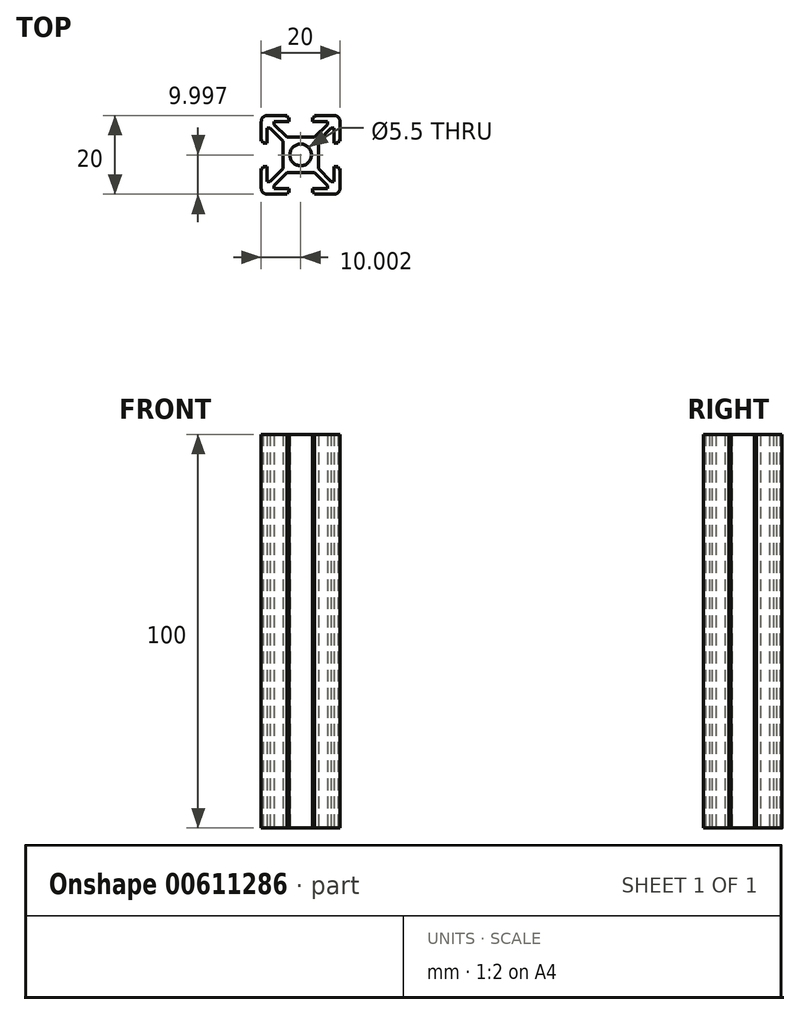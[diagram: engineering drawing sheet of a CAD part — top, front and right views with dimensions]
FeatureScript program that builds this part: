
annotation { "Feature Type Name" : "Feature", "Feature Type Description" : "" }
export const myFeature = defineFeature(function(context is Context, id is Id, definition is map)
    precondition{}
    {
        {
            var Q0;
            Q0=qCreatedBy(makeId("Top.planeOp"),FACE);
            var sketch = newSketch(context, id + "F0", { "sketchPlane" : qUnion([Q0])});
            skLineSegment(sketch, "E0", {"start": v(-1.2, -4.52) * mm, "end": v(-5.7, -4.52) * mm});
            skLineSegment(sketch, "E1", {"start": v(-8.97, -7.8) * mm, "end": v(-8.97, -8.52) * mm});
            skLineSegment(sketch, "E2", {"start": v(-8.97, -8.52) * mm, "end": v(-5.2, -8.52) * mm});
            skLineSegment(sketch, "E3", {"start": v(-5.2, -8.52) * mm, "end": v(-5.2, -9.52) * mm});
            skLineSegment(sketch, "E4", {"start": v(-7.76, -10.02) * mm, "end": v(-10.7, -10.02) * mm});
            skLineSegment(sketch, "E5", {"start": v(-5.2, -9.52) * mm, "end": v(-5.7, -9.52) * mm});
            skLineSegment(sketch, "E6", {"start": v(-5.7, -9.52) * mm, "end": v(-5.7, -10.02) * mm, "construction": true});
            skArc(sketch, "E7.filletArc", {"start": v(-11.76, -9.58) * mm, "mid": v(-11.27, -9.9) * mm, "end": v(-10.7, -10.02) * mm});
            skLineSegment(sketch, "E8", {"start": v(-5.7, -10.02) * mm, "end": v(-7.76, -10.02) * mm});
            skPoint(sketch, "E9.orphan", {"position": v(-2.2, -10.02) * mm});
            skLineSegment(sketch, "E10.trimOffspring", {"start": v(-10.7, -8.52) * mm, "end": v(-4.14, -1.97) * mm});
            skPoint(sketch, "E11", {"position": v(-2.2, -4.52) * mm});
            skLineSegment(sketch, "E12", {"start": v(-5.7, -4.52) * mm, "end": v(-8.97, -7.8) * mm});
            skArc(sketch, "E13", {"start": v(-4.14, -1.97) * mm, "mid": v(-3.25, -2.56) * mm, "end": v(-2.2, -2.77) * mm});
            skPoint(sketch, "E14", {"position": v(-4.14, -1.97) * mm});
            skLineSegment(sketch, "E15", {"start": v(-2.2, -4.02) * mm, "end": v(-2.2, -2.77) * mm});
            skLineSegment(sketch, "E16", {"start": v(-11.76, -9.58) * mm, "end": v(-10.7, -8.52) * mm});
            skPoint(sketch, "E17", {"position": v(-7.76, -10.02) * mm});
            skLineSegment(sketch, "E18", {"start": v(-5.7, -9.52) * mm, "end": v(-5.7, -10.02) * mm});
            skPoint(sketch, "E19.0.MirrorP", {"position": v(-12.2, -5.59) * mm});
            skPoint(sketch, "E19.1.MirrorP", {"position": v(-12.2, -5.59) * mm});
            skPoint(sketch, "E19.2.MirrorP", {"position": v(-12.2, -5.59) * mm});
            skPoint(sketch, "E19.3.MirrorP", {"position": v(-12.2, -5.59) * mm});
            skPoint(sketch, "E19.4.MirrorP", {"position": v(-12.2, -5.59) * mm});
            skPoint(sketch, "E19.5.MirrorP", {"position": v(-12.2, -5.59) * mm});
            skPoint(sketch, "E19.6.MirrorP", {"position": v(-12.2, -5.59) * mm});
            skPoint(sketch, "E19.7.MirrorP", {"position": v(-12.2, -5.59) * mm});
            skPoint(sketch, "E19.8.MirrorP", {"position": v(-12.2, -5.59) * mm});
            skPoint(sketch, "E19.9.MirrorP", {"position": v(-12.2, -5.59) * mm});
            skPoint(sketch, "E19.10.MirrorP", {"position": v(-12.2, -5.59) * mm});
            skLineSegment(sketch, "E19.11.MirrorCS", {"start": v(-11.7, -3.52) * mm, "end": v(-12.2, -3.52) * mm, "construction": true});
            skPoint(sketch, "E19.12.MirrorP", {"position": v(-12.2, -5.59) * mm});
            skLineSegment(sketch, "E19.13.MirrorCS", {"start": v(-11.7, -3.52) * mm, "end": v(-12.2, -3.52) * mm});
            skLineSegment(sketch, "E19.14.MirrorCS", {"start": v(-9.97, -6.8) * mm, "end": v(-10.7, -6.8) * mm});
            skPoint(sketch, "E19.15.MirrorP", {"position": v(-12.2, -5.59) * mm});
            skLineSegment(sketch, "E19.16.MirrorCS", {"start": v(-11.7, -3.02) * mm, "end": v(-11.7, -3.52) * mm});
            skPoint(sketch, "E19.17.MirrorP", {"position": v(-12.2, -0.02) * mm});
            skLineSegment(sketch, "E19.18.MirrorCS", {"start": v(-12.2, -5.59) * mm, "end": v(-12.2, -8.52) * mm});
            skArc(sketch, "E19.19.MirrorCS", {"start": v(-4.14, -1.97) * mm, "mid": v(-4.74, -1.07) * mm, "end": v(-4.95, -0.02) * mm});
            skPoint(sketch, "E19.20.MirrorP", {"position": v(-6.7, -0.02) * mm});
            skLineSegment(sketch, "E19.21.MirrorCS", {"start": v(-6.7, -3.52) * mm, "end": v(-9.97, -6.8) * mm});
            skLineSegment(sketch, "E19.23.MirrorCS", {"start": v(-6.7, -1.02) * mm, "end": v(-6.7, -3.52) * mm});
            skLineSegment(sketch, "E19.24.MirrorCS", {"start": v(-10.7, -6.8) * mm, "end": v(-10.7, -3.02) * mm});
            skLineSegment(sketch, "E19.25.MirrorCS", {"start": v(-12.2, -3.52) * mm, "end": v(-12.2, -5.59) * mm});
            skArc(sketch, "E19.28.MirrorCS", {"start": v(-11.76, -9.58) * mm, "mid": v(-12.08, -9.1) * mm, "end": v(-12.2, -8.52) * mm});
            skLineSegment(sketch, "E19.30.MirrorCS", {"start": v(-12.2, -5.59) * mm, "end": v(-12.2, -8.52) * mm});
            skPoint(sketch, "E19.31.MirrorP", {"position": v(-12.2, -5.59) * mm});
            skLineSegment(sketch, "E19.32.MirrorCS", {"start": v(-10.7, -3.02) * mm, "end": v(-11.7, -3.02) * mm});
            skPoint(sketch, "E20.0.MirrorP", {"position": v(-7.76, 9.98) * mm});
            skPoint(sketch, "E20.1.MirrorP", {"position": v(-12.2, 5.54) * mm});
            skPoint(sketch, "E20.2.MirrorP", {"position": v(-7.76, 9.98) * mm});
            skPoint(sketch, "E20.3.MirrorP", {"position": v(-12.2, 5.54) * mm});
            skPoint(sketch, "E20.4.MirrorP", {"position": v(-7.76, 9.98) * mm});
            skPoint(sketch, "E20.5.MirrorP", {"position": v(-12.2, 5.54) * mm});
            skPoint(sketch, "E20.6.MirrorP", {"position": v(-12.2, 5.54) * mm});
            skPoint(sketch, "E20.7.MirrorP", {"position": v(-7.76, 9.98) * mm});
            skPoint(sketch, "E20.8.MirrorP", {"position": v(-7.76, 9.98) * mm});
            skPoint(sketch, "E20.9.MirrorP", {"position": v(-12.2, 5.54) * mm});
            skPoint(sketch, "E20.10.MirrorP", {"position": v(-7.76, 9.98) * mm});
            skPoint(sketch, "E20.11.MirrorP", {"position": v(-12.2, 5.54) * mm});
            skPoint(sketch, "E20.12.MirrorP", {"position": v(-7.76, 9.98) * mm});
            skPoint(sketch, "E20.13.MirrorP", {"position": v(-12.2, 5.54) * mm});
            skPoint(sketch, "E20.14.MirrorP", {"position": v(-7.76, 9.98) * mm});
            skPoint(sketch, "E20.15.MirrorP", {"position": v(-12.2, 5.54) * mm});
            skPoint(sketch, "E20.16.MirrorP", {"position": v(-7.76, 9.98) * mm});
            skPoint(sketch, "E20.17.MirrorP", {"position": v(-12.2, 5.54) * mm});
            skLineSegment(sketch, "E20.18.MirrorCS", {"start": v(-11.7, 3.48) * mm, "end": v(-12.2, 3.48) * mm, "construction": true});
            skPoint(sketch, "E20.19.MirrorP", {"position": v(-7.76, 9.98) * mm});
            skPoint(sketch, "E20.20.MirrorP", {"position": v(-12.2, 5.54) * mm});
            skLineSegment(sketch, "E20.21.MirrorCS", {"start": v(-5.7, 9.48) * mm, "end": v(-5.7, 9.98) * mm, "construction": true});
            skLineSegment(sketch, "E20.22.MirrorCS", {"start": v(-5.7, 9.48) * mm, "end": v(-5.7, 9.98) * mm});
            skPoint(sketch, "E20.23.MirrorP", {"position": v(-7.76, 9.98) * mm});
            skLineSegment(sketch, "E20.24.MirrorCS", {"start": v(-11.7, 3.48) * mm, "end": v(-12.2, 3.48) * mm});
            skPoint(sketch, "E20.25.MirrorP", {"position": v(-12.2, 5.54) * mm});
            skPoint(sketch, "E20.26.MirrorP", {"position": v(-7.76, 9.98) * mm});
            skPoint(sketch, "E20.27.MirrorP", {"position": v(-12.2, 5.54) * mm});
            skLineSegment(sketch, "E20.28.MirrorCS", {"start": v(-5.2, 9.48) * mm, "end": v(-5.7, 9.48) * mm});
            skLineSegment(sketch, "E20.29.MirrorCS", {"start": v(-11.7, 2.98) * mm, "end": v(-11.7, 3.48) * mm});
            skLineSegment(sketch, "E20.30.MirrorCS", {"start": v(-10.7, 2.98) * mm, "end": v(-11.7, 2.98) * mm});
            skPoint(sketch, "E20.31.MirrorP", {"position": v(-7.76, 9.98) * mm});
            skPoint(sketch, "E20.32.MirrorP", {"position": v(-12.2, 5.54) * mm});
            skLineSegment(sketch, "E20.34.MirrorCS", {"start": v(-12.2, 3.48) * mm, "end": v(-12.2, 5.54) * mm});
            skArc(sketch, "E20.35.MirrorCS", {"start": v(-11.76, 9.54) * mm, "mid": v(-12.08, 9.05) * mm, "end": v(-12.2, 8.48) * mm});
            skLineSegment(sketch, "E20.36.MirrorCS", {"start": v(-10.7, 6.75) * mm, "end": v(-10.7, 2.98) * mm});
            skLineSegment(sketch, "E20.38.MirrorCS", {"start": v(-12.2, 5.54) * mm, "end": v(-12.2, 8.48) * mm});
            skLineSegment(sketch, "E20.39.MirrorCS", {"start": v(-6.2, -0.02) * mm, "end": v(-4.95, -0.02) * mm});
            skLineSegment(sketch, "E20.40.MirrorCS", {"start": v(-6.7, 3.48) * mm, "end": v(-9.97, 6.75) * mm});
            skLineSegment(sketch, "E20.41.MirrorCS", {"start": v(-6.7, -1.02) * mm, "end": v(-6.7, 3.48) * mm});
            skLineSegment(sketch, "E20.42.MirrorCS", {"start": v(-3.2, 4.48) * mm, "end": v(-5.7, 4.48) * mm});
            skLineSegment(sketch, "E20.43.MirrorCS", {"start": v(-8.97, 8.48) * mm, "end": v(-5.2, 8.48) * mm});
            skLineSegment(sketch, "E20.44.MirrorCS", {"start": v(-8.97, 7.75) * mm, "end": v(-8.97, 8.48) * mm});
            skLineSegment(sketch, "E20.45.MirrorCS", {"start": v(-7.76, 9.98) * mm, "end": v(-10.7, 9.98) * mm});
            skLineSegment(sketch, "E20.46.MirrorCS", {"start": v(-5.2, 8.48) * mm, "end": v(-5.2, 9.48) * mm});
            skLineSegment(sketch, "E20.48.MirrorCS", {"start": v(-7.76, 9.98) * mm, "end": v(-10.7, 9.98) * mm});
            skLineSegment(sketch, "E20.49.MirrorCS", {"start": v(-5.7, 9.98) * mm, "end": v(-7.76, 9.98) * mm});
            skArc(sketch, "E20.50.MirrorCS", {"start": v(-11.76, 9.54) * mm, "mid": v(-11.27, 9.86) * mm, "end": v(-10.7, 9.98) * mm});
            skLineSegment(sketch, "E20.51.MirrorCS", {"start": v(-5.7, 4.48) * mm, "end": v(-8.97, 7.75) * mm});
            skLineSegment(sketch, "E20.52.MirrorCS", {"start": v(-10.7, 8.48) * mm, "end": v(-4.14, 1.92) * mm});
            skLineSegment(sketch, "E20.53.MirrorCS", {"start": v(-11.76, 9.54) * mm, "end": v(-10.7, 8.48) * mm});
            skLineSegment(sketch, "E20.54.MirrorCS", {"start": v(-11.76, 9.54) * mm, "end": v(-10.7, 8.48) * mm});
            skLineSegment(sketch, "E20.55.MirrorCS", {"start": v(-2.2, 3.98) * mm, "end": v(-2.2, 2.73) * mm});
            skArc(sketch, "E20.56.MirrorCS", {"start": v(-4.14, 1.92) * mm, "mid": v(-3.25, 2.52) * mm, "end": v(-2.2, 2.73) * mm});
            skLineSegment(sketch, "E20.59.MirrorCS", {"start": v(-9.97, 6.75) * mm, "end": v(-10.7, 6.75) * mm});
            skPoint(sketch, "E20.60.MirrorP", {"position": v(-7.76, 9.98) * mm});
            skArc(sketch, "E20.61.MirrorCS", {"start": v(-4.14, 1.92) * mm, "mid": v(-4.74, 1.03) * mm, "end": v(-4.95, -0.02) * mm});
            skPoint(sketch, "E20.63.MirrorP", {"position": v(-4.14, 1.92) * mm});
            skPoint(sketch, "E20.64.MirrorP", {"position": v(-4.14, 1.92) * mm});
            skLineSegment(sketch, "E20.65.MirrorCS", {"start": v(-12.2, 5.54) * mm, "end": v(-12.2, 8.48) * mm});
            skPoint(sketch, "E20.66.MirrorP", {"position": v(-12.2, 5.54) * mm});
            skPoint(sketch, "E21.0.MirrorP", {"position": v(7.8, 5.54) * mm});
            skPoint(sketch, "E21.1.MirrorP", {"position": v(3.37, -10.02) * mm});
            skPoint(sketch, "E21.2.MirrorP", {"position": v(3.37, 9.98) * mm});
            skPoint(sketch, "E21.3.MirrorP", {"position": v(7.8, 5.54) * mm});
            skPoint(sketch, "E21.4.MirrorP", {"position": v(7.8, -5.59) * mm});
            skPoint(sketch, "E21.5.MirrorP", {"position": v(3.37, -10.02) * mm});
            skPoint(sketch, "E21.6.MirrorP", {"position": v(3.37, -10.02) * mm});
            skPoint(sketch, "E21.7.MirrorP", {"position": v(7.8, 5.54) * mm});
            skPoint(sketch, "E21.8.MirrorP", {"position": v(3.37, 9.98) * mm});
            skPoint(sketch, "E21.9.MirrorP", {"position": v(7.8, -5.59) * mm});
            skPoint(sketch, "E21.10.MirrorP", {"position": v(7.8, 5.54) * mm});
            skPoint(sketch, "E21.11.MirrorP", {"position": v(3.37, -10.02) * mm});
            skPoint(sketch, "E21.12.MirrorP", {"position": v(3.37, 9.98) * mm});
            skPoint(sketch, "E21.13.MirrorP", {"position": v(7.8, -5.59) * mm});
            skPoint(sketch, "E21.14.MirrorP", {"position": v(7.8, 5.54) * mm});
            skPoint(sketch, "E21.15.MirrorP", {"position": v(3.37, -10.02) * mm});
            skPoint(sketch, "E21.16.MirrorP", {"position": v(7.8, -5.59) * mm});
            skPoint(sketch, "E21.17.MirrorP", {"position": v(3.37, 9.98) * mm});
            skPoint(sketch, "E21.18.MirrorP", {"position": v(3.37, -10.02) * mm});
            skPoint(sketch, "E21.19.MirrorP", {"position": v(3.37, 9.98) * mm});
            skPoint(sketch, "E21.20.MirrorP", {"position": v(7.8, 5.54) * mm});
            skPoint(sketch, "E21.21.MirrorP", {"position": v(7.8, -5.59) * mm});
            skPoint(sketch, "E21.22.MirrorP", {"position": v(7.8, -5.59) * mm});
            skPoint(sketch, "E21.23.MirrorP", {"position": v(3.37, -10.02) * mm});
            skPoint(sketch, "E21.24.MirrorP", {"position": v(7.8, 5.54) * mm});
            skPoint(sketch, "E21.25.MirrorP", {"position": v(3.37, 9.98) * mm});
            skPoint(sketch, "E21.26.MirrorP", {"position": v(7.8, -5.59) * mm});
            skPoint(sketch, "E21.27.MirrorP", {"position": v(7.8, 5.54) * mm});
            skPoint(sketch, "E21.28.MirrorP", {"position": v(3.37, -10.02) * mm});
            skPoint(sketch, "E21.29.MirrorP", {"position": v(3.37, 9.98) * mm});
            skPoint(sketch, "E21.30.MirrorP", {"position": v(7.8, -5.59) * mm});
            skPoint(sketch, "E21.31.MirrorP", {"position": v(3.37, 9.98) * mm});
            skPoint(sketch, "E21.32.MirrorP", {"position": v(3.37, -10.02) * mm});
            skPoint(sketch, "E21.33.MirrorP", {"position": v(7.8, 5.54) * mm});
            skPoint(sketch, "E21.34.MirrorP", {"position": v(7.8, 5.54) * mm});
            skPoint(sketch, "E21.35.MirrorP", {"position": v(3.37, 9.98) * mm});
            skPoint(sketch, "E21.36.MirrorP", {"position": v(7.8, -5.59) * mm});
            skPoint(sketch, "E21.37.MirrorP", {"position": v(3.37, -10.02) * mm});
            skLineSegment(sketch, "E21.38.MirrorCS", {"start": v(1.3, 9.48) * mm, "end": v(1.3, 9.98) * mm, "construction": true});
            skLineSegment(sketch, "E21.39.MirrorCS", {"start": v(7.3, 3.48) * mm, "end": v(7.8, 3.48) * mm, "construction": true});
            skLineSegment(sketch, "E21.40.MirrorCS", {"start": v(7.3, -3.52) * mm, "end": v(7.8, -3.52) * mm, "construction": true});
            skLineSegment(sketch, "E21.41.MirrorCS", {"start": v(1.3, -9.52) * mm, "end": v(1.3, -10.02) * mm, "construction": true});
            skPoint(sketch, "E21.42.MirrorP", {"position": v(7.8, 5.54) * mm});
            skPoint(sketch, "E21.43.MirrorP", {"position": v(7.8, -5.59) * mm});
            skPoint(sketch, "E21.44.MirrorP", {"position": v(3.37, -10.02) * mm});
            skPoint(sketch, "E21.45.MirrorP", {"position": v(3.37, 9.98) * mm});
            skLineSegment(sketch, "E21.46.MirrorCS", {"start": v(7.3, 3.48) * mm, "end": v(7.8, 3.48) * mm});
            skLineSegment(sketch, "E21.47.MirrorCS", {"start": v(7.3, -3.02) * mm, "end": v(7.3, -3.52) * mm});
            skLineSegment(sketch, "E21.48.MirrorCS", {"start": v(7.3, -3.52) * mm, "end": v(7.8, -3.52) * mm});
            skLineSegment(sketch, "E21.49.MirrorCS", {"start": v(7.36, -9.58) * mm, "end": v(6.3, -8.52) * mm});
            skLineSegment(sketch, "E21.50.MirrorCS", {"start": v(0.8, -9.52) * mm, "end": v(1.3, -9.52) * mm});
            skPoint(sketch, "E21.51.MirrorP", {"position": v(7.8, -5.59) * mm});
            skPoint(sketch, "E21.52.MirrorP", {"position": v(7.8, 5.54) * mm});
            skPoint(sketch, "E21.53.MirrorP", {"position": v(3.37, 9.98) * mm});
            skPoint(sketch, "E21.54.MirrorP", {"position": v(3.37, -10.02) * mm});
            skLineSegment(sketch, "E21.55.MirrorCS", {"start": v(0.8, 9.48) * mm, "end": v(1.3, 9.48) * mm});
            skLineSegment(sketch, "E21.56.MirrorCS", {"start": v(7.3, 2.98) * mm, "end": v(7.3, 3.48) * mm});
            skLineSegment(sketch, "E21.57.MirrorCS", {"start": v(1.3, -9.52) * mm, "end": v(1.3, -10.02) * mm});
            skLineSegment(sketch, "E21.58.MirrorCS", {"start": v(1.3, 9.48) * mm, "end": v(1.3, 9.98) * mm});
            skLineSegment(sketch, "E21.59.MirrorCS", {"start": v(0.8, 8.48) * mm, "end": v(0.8, 9.48) * mm});
            skLineSegment(sketch, "E21.60.MirrorCS", {"start": v(4.57, 7.75) * mm, "end": v(4.57, 8.48) * mm});
            skPoint(sketch, "E21.61.MirrorP", {"position": v(3.37, 9.98) * mm});
            skLineSegment(sketch, "E21.62.MirrorCS", {"start": v(4.57, -7.8) * mm, "end": v(4.57, -8.52) * mm});
            skPoint(sketch, "E21.63.MirrorP", {"position": v(3.37, -10.02) * mm});
            skPoint(sketch, "E21.64.MirrorP", {"position": v(7.8, -5.59) * mm});
            skLineSegment(sketch, "E21.65.MirrorCS", {"start": v(7.36, -9.58) * mm, "end": v(6.3, -8.52) * mm});
            skLineSegment(sketch, "E21.66.MirrorCS", {"start": v(5.57, 6.75) * mm, "end": v(6.3, 6.75) * mm});
            skLineSegment(sketch, "E21.69.MirrorCS", {"start": v(1.8, -0.02) * mm, "end": v(0.55, -0.02) * mm});
            skLineSegment(sketch, "E21.71.MirrorCS", {"start": v(7.8, 5.54) * mm, "end": v(7.8, 8.48) * mm});
            skPoint(sketch, "E21.72.MirrorP", {"position": v(7.8, 5.54) * mm});
            skPoint(sketch, "E21.73.MirrorP", {"position": v(7.8, -0.02) * mm});
            skLineSegment(sketch, "E21.74.MirrorCS", {"start": v(7.36, 9.54) * mm, "end": v(6.3, 8.48) * mm});
            skLineSegment(sketch, "E21.76.MirrorCS", {"start": v(5.57, -6.8) * mm, "end": v(6.3, -6.8) * mm});
            skLineSegment(sketch, "E21.78.MirrorCS", {"start": v(7.8, 5.54) * mm, "end": v(7.8, 8.48) * mm});
            skLineSegment(sketch, "E21.79.MirrorCS", {"start": v(1.3, -10.02) * mm, "end": v(3.37, -10.02) * mm});
            skLineSegment(sketch, "E21.80.MirrorCS", {"start": v(0.8, -8.52) * mm, "end": v(0.8, -9.52) * mm});
            skLineSegment(sketch, "E21.81.MirrorCS", {"start": v(3.37, -10.02) * mm, "end": v(6.3, -10.02) * mm});
            skPoint(sketch, "E21.82.MirrorP", {"position": v(-2.2, 4.48) * mm});
            skPoint(sketch, "E21.83.MirrorP", {"position": v(3.37, -10.02) * mm});
            skLineSegment(sketch, "E21.84.MirrorCS", {"start": v(6.3, 2.98) * mm, "end": v(7.3, 2.98) * mm});
            skLineSegment(sketch, "E21.85.MirrorCS", {"start": v(1.3, 9.98) * mm, "end": v(3.37, 9.98) * mm});
            skArc(sketch, "E21.86.MirrorCS", {"start": v(-0.25, -1.97) * mm, "mid": v(-1.15, -2.56) * mm, "end": v(-2.2, -2.77) * mm});
            skPoint(sketch, "E21.87.MirrorP", {"position": v(-0.25, -1.97) * mm});
            skPoint(sketch, "E21.88.MirrorP", {"position": v(2.3, -0.02) * mm});
            skArc(sketch, "E21.89.MirrorCS", {"start": v(7.36, 9.54) * mm, "mid": v(6.88, 9.86) * mm, "end": v(6.3, 9.98) * mm});
            skLineSegment(sketch, "E21.90.MirrorCS", {"start": v(7.8, 3.48) * mm, "end": v(7.8, 5.54) * mm});
            skLineSegment(sketch, "E21.91.MirrorCS", {"start": v(6.3, -8.52) * mm, "end": v(-0.25, -1.97) * mm});
            skLineSegment(sketch, "E21.92.MirrorCS", {"start": v(1.3, -4.52) * mm, "end": v(4.57, -7.8) * mm});
            skArc(sketch, "E21.93.MirrorCS", {"start": v(7.36, -9.58) * mm, "mid": v(6.88, -9.9) * mm, "end": v(6.3, -10.02) * mm});
            skLineSegment(sketch, "E21.94.MirrorCS", {"start": v(4.57, 8.48) * mm, "end": v(0.8, 8.48) * mm});
            skLineSegment(sketch, "E21.95.MirrorCS", {"start": v(2.3, 0.98) * mm, "end": v(2.3, 3.48) * mm});
            skLineSegment(sketch, "E21.96.MirrorCS", {"start": v(7.8, -5.59) * mm, "end": v(7.8, -8.52) * mm});
            skLineSegment(sketch, "E21.97.MirrorCS", {"start": v(3.37, -10.02) * mm, "end": v(6.3, -10.02) * mm});
            skPoint(sketch, "E21.99.MirrorP", {"position": v(3.37, 9.98) * mm});
            skPoint(sketch, "E21.100.MirrorP", {"position": v(-2.2, 9.98) * mm});
            skLineSegment(sketch, "E21.101.MirrorCS", {"start": v(7.8, -5.59) * mm, "end": v(7.8, -8.52) * mm});
            skPoint(sketch, "E21.103.MirrorP", {"position": v(2.3, -0.02) * mm});
            skArc(sketch, "E21.104.MirrorCS", {"start": v(-0.25, 1.92) * mm, "mid": v(-1.15, 2.52) * mm, "end": v(-2.2, 2.73) * mm});
            skArc(sketch, "E21.105.MirrorCS", {"start": v(-0.25, -1.97) * mm, "mid": v(0.34, -1.07) * mm, "end": v(0.55, -0.02) * mm});
            skLineSegment(sketch, "E21.106.MirrorCS", {"start": v(2.3, 3.48) * mm, "end": v(5.57, 6.75) * mm});
            skLineSegment(sketch, "E21.107.MirrorCS", {"start": v(6.3, 8.48) * mm, "end": v(-0.25, 1.92) * mm});
            skLineSegment(sketch, "E21.108.MirrorCS", {"start": v(6.3, -6.8) * mm, "end": v(6.3, -3.02) * mm});
            skArc(sketch, "E21.109.MirrorCS", {"start": v(7.36, -9.58) * mm, "mid": v(7.69, -9.1) * mm, "end": v(7.8, -8.52) * mm});
            skPoint(sketch, "E21.110.MirrorP", {"position": v(-0.25, 1.92) * mm});
            skLineSegment(sketch, "E21.111.MirrorCS", {"start": v(4.57, -8.52) * mm, "end": v(0.8, -8.52) * mm});
            skLineSegment(sketch, "E21.112.MirrorCS", {"start": v(-1.2, -4.52) * mm, "end": v(1.3, -4.52) * mm});
            skLineSegment(sketch, "E21.113.MirrorCS", {"start": v(2.3, 0.98) * mm, "end": v(2.3, -1.02) * mm});
            skLineSegment(sketch, "E21.114.MirrorCS", {"start": v(1.3, 4.48) * mm, "end": v(4.57, 7.75) * mm});
            skPoint(sketch, "E21.115.MirrorP", {"position": v(7.8, -5.59) * mm});
            skLineSegment(sketch, "E21.116.MirrorCS", {"start": v(7.36, 9.54) * mm, "end": v(6.3, 8.48) * mm});
            skLineSegment(sketch, "E21.117.MirrorCS", {"start": v(1.8, -0.02) * mm, "end": v(0.55, -0.02) * mm});
            skArc(sketch, "E21.118.MirrorCS", {"start": v(7.36, 9.54) * mm, "mid": v(7.69, 9.05) * mm, "end": v(7.8, 8.48) * mm});
            skPoint(sketch, "E21.119.MirrorP", {"position": v(3.37, 9.98) * mm});
            skLineSegment(sketch, "E21.120.MirrorCS", {"start": v(6.3, -3.02) * mm, "end": v(7.3, -3.02) * mm});
            skLineSegment(sketch, "E21.121.MirrorCS", {"start": v(-1.2, 4.48) * mm, "end": v(1.3, 4.48) * mm});
            skArc(sketch, "E21.122.MirrorCS", {"start": v(-0.25, 1.92) * mm, "mid": v(0.34, 1.03) * mm, "end": v(0.55, -0.02) * mm});
            skLineSegment(sketch, "E21.123.MirrorCS", {"start": v(3.37, 9.98) * mm, "end": v(6.3, 9.98) * mm});
            skPoint(sketch, "E21.124.MirrorP", {"position": v(7.8, -0.02) * mm});
            skLineSegment(sketch, "E21.125.MirrorCS", {"start": v(7.8, -3.52) * mm, "end": v(7.8, -5.59) * mm});
            skLineSegment(sketch, "E21.126.MirrorCS", {"start": v(3.37, 9.98) * mm, "end": v(6.3, 9.98) * mm});
            skLineSegment(sketch, "E21.127.MirrorCS", {"start": v(2.3, -3.52) * mm, "end": v(5.57, -6.8) * mm});
            skPoint(sketch, "E21.128.MirrorP", {"position": v(7.8, -5.59) * mm});
            skPoint(sketch, "E21.129.MirrorP", {"position": v(-0.25, -1.97) * mm});
            skPoint(sketch, "E21.131.MirrorP", {"position": v(-0.25, 1.92) * mm});
            skLineSegment(sketch, "E21.132.MirrorCS", {"start": v(6.3, 6.75) * mm, "end": v(6.3, 2.98) * mm});
            skPoint(sketch, "E21.133.MirrorP", {"position": v(7.8, 5.54) * mm});
            skLineSegment(sketch, "E22.113.MirrorCS", {"start": v(2.3, -1.02) * mm, "end": v(2.3, -3.52) * mm});
            skLineSegment(sketch, "E22.121.MirrorCS", {"start": v(-3.2, 4.48) * mm, "end": v(1.3, 4.48) * mm});
            skPoint(sketch, "E23.orphan", {"position": v(-3.2, -4.52) * mm});
            skSolve(sketch);
        }
        {
            var Q0;
            Q0=makeQuery(id+"F0.imprint","IMPRINT",FACE,{"disambiguationData":[TD([[makeQuery(id+"F0.imprint","IMPRINT",EDGE,{"derivedFrom":sQuery(id+"F0.wireOp",EDGE,"E0")}),-1.0]])]});
            var Q1;
            Q1=makeQuery(id+"F0.imprint","IMPRINT",FACE,{"disambiguationData":[TD([[makeQuery(id+"F0.imprint","IMPRINT",EDGE,{"derivedFrom":sQuery(id+"F0.wireOp",EDGE,"E10.trimOffspring")}),1.0]])]});
            var Q2;
            Q2=makeQuery(id+"F0.imprint","IMPRINT",FACE,{"disambiguationData":[TD([[makeQuery(id+"F0.imprint","IMPRINT",EDGE,{"derivedFrom":sQuery(id+"F0.wireOp",EDGE,"E20.22.MirrorCS")}),1.0]])]});
            var Q3;
            Q3=makeQuery(id+"F0.imprint","IMPRINT",FACE,{"disambiguationData":[TD([[makeQuery(id+"F0.imprint","IMPRINT",EDGE,{"derivedFrom":sQuery(id+"F0.wireOp",EDGE,"E21.113.MirrorCS")}),-1.0]])]});
            extrude(context, id + "F1", {"entities" : qUnion([Q0, Q1, Q2, Q3]), "depth" : 100 * mm, "offsetDistance" : 25.4 * mm});
        }
    });
